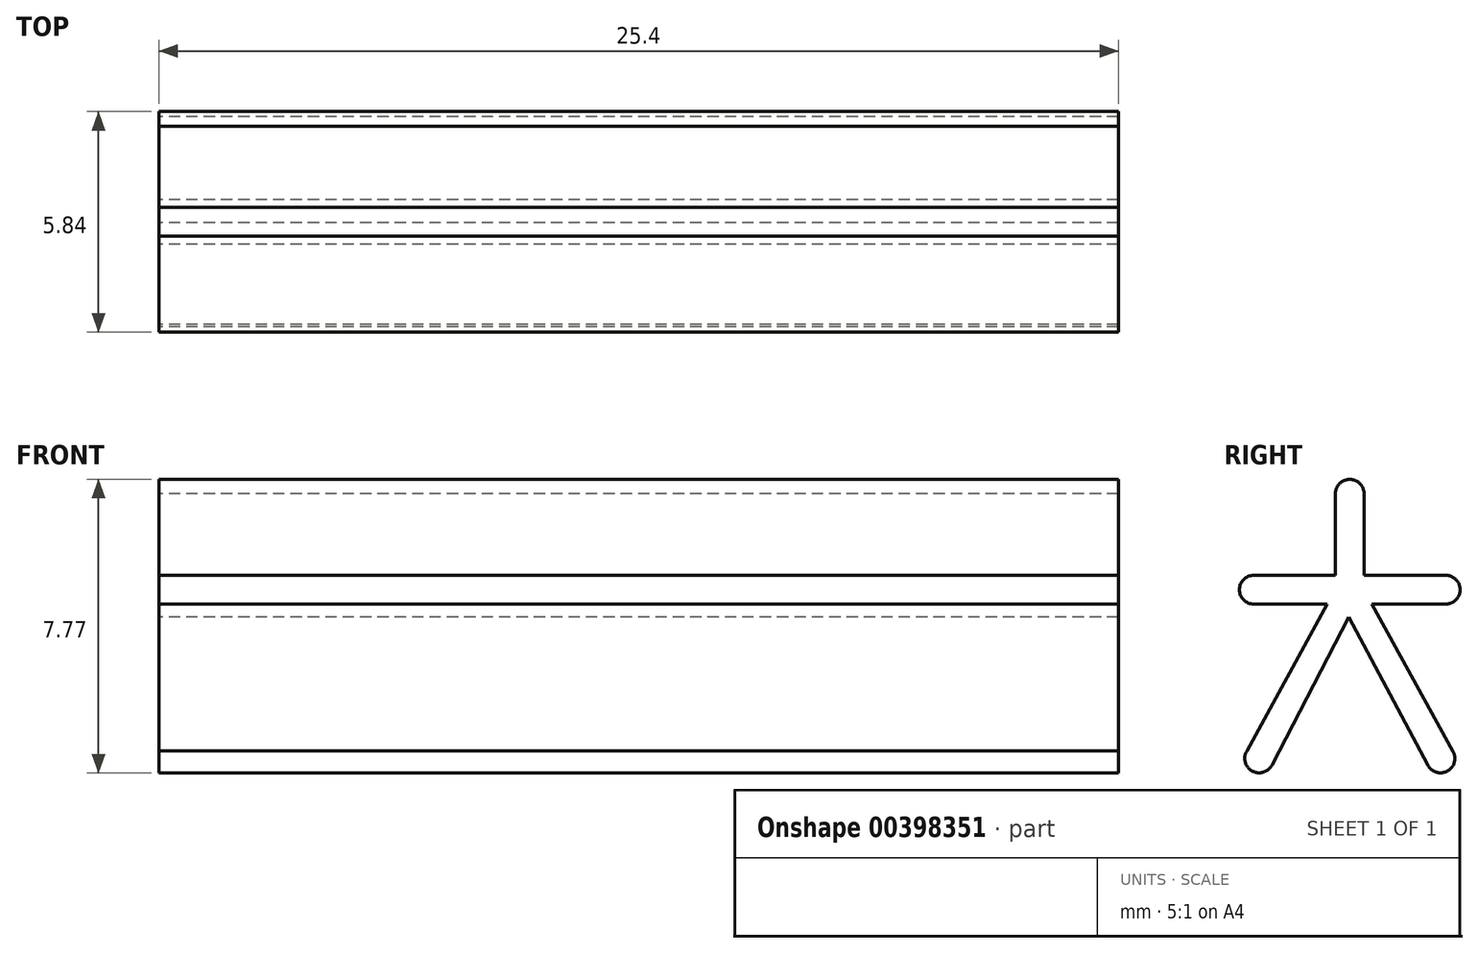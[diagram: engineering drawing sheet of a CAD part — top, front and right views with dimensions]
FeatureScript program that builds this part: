
annotation { "Feature Type Name" : "Feature", "Feature Type Description" : "" }
export const myFeature = defineFeature(function(context is Context, id is Id, definition is map)
    precondition{}
    {
        {
            var Q0;
            Q0=qCreatedBy(makeId("Right.planeOp"),FACE);
            var sketch = newSketch(context, id + "F0", { "sketchPlane" : qUnion([Q0])});
            skLineSegment(sketch, "E0", {"start": v(0, 0) * mm, "end": v(0, 2.54) * mm});
            skLineSegment(sketch, "E1", {"start": v(0, 0) * mm, "end": v(2.54, 0) * mm});
            skLineSegment(sketch, "E2", {"start": v(0, 0) * mm, "end": v(-2.54, 0) * mm});
            skLineSegment(sketch, "E3", {"start": v(0, 0) * mm, "end": v(-2.4, -4.47) * mm});
            skLineSegment(sketch, "E4", {"start": v(0, 0) * mm, "end": v(2.4, -4.47) * mm});
            skCircle(sketch, "E5", {"center": v(0, 0) * mm, "radius": 0.38 * mm});
            skCircle(sketch, "E6", {"center": v(0, 2.54) * mm, "radius": 0.38 * mm});
            skCircle(sketch, "E7", {"center": v(2.54, 0) * mm, "radius": 0.38 * mm});
            skCircle(sketch, "E8", {"center": v(2.4, -4.47) * mm, "radius": 0.38 * mm});
            skCircle(sketch, "E9", {"center": v(-2.4, -4.47) * mm, "radius": 0.38 * mm});
            skCircle(sketch, "E10", {"center": v(-2.54, 0) * mm, "radius": 0.38 * mm});
            skLineSegment(sketch, "E11", {"start": v(0.38, 2.53) * mm, "end": v(0.38, 0) * mm});
            skLineSegment(sketch, "E12", {"start": v(-0.38, 2.54) * mm, "end": v(-0.38, 0) * mm});
            skLineSegment(sketch, "E13", {"start": v(2.53, 0.38) * mm, "end": v(0, 0.38) * mm});
            skLineSegment(sketch, "E14", {"start": v(0, -0.38) * mm, "end": v(2.54, -0.38) * mm});
            skLineSegment(sketch, "E15", {"start": v(0, -0.38) * mm, "end": v(-2.54, -0.38) * mm});
            skLineSegment(sketch, "E16", {"start": v(0, 0.38) * mm, "end": v(-2.54, 0.38) * mm});
            skLineSegment(sketch, "E17", {"start": v(-2.72, -4.26) * mm, "end": v(-0.38, 0) * mm});
            skLineSegment(sketch, "E18", {"start": v(0.38, 0) * mm, "end": v(2.74, -4.28) * mm});
            skLineSegment(sketch, "E19", {"start": v(-0.2, -0.38) * mm, "end": v(2.07, -4.65) * mm});
            skLineSegment(sketch, "E20", {"start": v(0.18, -0.34) * mm, "end": v(-2.06, -4.65) * mm});
            skSolve(sketch);
        }
        {
            var Q0;
            {var subQ3=sQuery(id+"F0.wireOp",EDGE,"E7");var subQ5=sQuery(id+"F0.wireOp",EDGE,"E14");var subQ6=makeQuery(id+"F0.imprint","INTERSECT",VERTEX,{"derivedFrom":[subQ3,subQ5]});Q0=makeQuery(id+"F0.imprint","IMPRINT",FACE,{"disambiguationData":[TD([[makeQuery(id+"F0.imprint","IMPRINT",EDGE,{"disambiguationData":[TD([[subQ6,1.0]])],"derivedFrom":subQ3}),-1.0]])]});}
            var Q1;
            {var subQ3=sQuery(id+"F0.wireOp",EDGE,"E10");var subQ5=sQuery(id+"F0.wireOp",EDGE,"E16");var subQ6=makeQuery(id+"F0.imprint","INTERSECT",VERTEX,{"derivedFrom":[subQ3,subQ5]});Q1=makeQuery(id+"F0.imprint","IMPRINT",FACE,{"disambiguationData":[TD([[makeQuery(id+"F0.imprint","IMPRINT",EDGE,{"disambiguationData":[TD([[subQ6,1.0]])],"derivedFrom":subQ3}),-1.0]])]});}
            var Q2;
            {var subQ3=sQuery(id+"F0.wireOp",EDGE,"E10");var subQ5=sQuery(id+"F0.wireOp",EDGE,"E15");var subQ6=makeQuery(id+"F0.imprint","INTERSECT",VERTEX,{"derivedFrom":[subQ3,subQ5]});Q2=makeQuery(id+"F0.imprint","IMPRINT",FACE,{"disambiguationData":[TD([[makeQuery(id+"F0.imprint","IMPRINT",EDGE,{"disambiguationData":[TD([[subQ6,-1.0]])],"derivedFrom":subQ3}),-1.0]])]});}
            var Q3;
            {var subQ3=sQuery(id+"F0.wireOp",EDGE,"E7");var subQ5=sQuery(id+"F0.wireOp",EDGE,"E13");var subQ6=makeQuery(id+"F0.imprint","INTERSECT",VERTEX,{"derivedFrom":[subQ3,subQ5]});Q3=makeQuery(id+"F0.imprint","IMPRINT",FACE,{"disambiguationData":[TD([[makeQuery(id+"F0.imprint","IMPRINT",EDGE,{"disambiguationData":[TD([[subQ6,-1.0]])],"derivedFrom":subQ3}),-1.0]])]});}
            var Q4;
            {var subQ0=sQuery(id+"F0.wireOp",EDGE,"E8");var subQ1=sQuery(id+"F0.wireOp",EDGE,"E4");var subQ2=makeQuery(id+"F0.imprint","INTERSECT",VERTEX,{"derivedFrom":[subQ1,subQ0]});Q4=makeQuery(id+"F0.imprint","IMPRINT",FACE,{"disambiguationData":[TD([[makeQuery(id+"F0.imprint","IMPRINT",EDGE,{"disambiguationData":[TD([[subQ2,1.0]])],"derivedFrom":subQ1}),1.0]])]});}
            var Q5;
            {var subQ3=sQuery(id+"F0.wireOp",EDGE,"E14");var subQ5=sQuery(id+"F0.wireOp",EDGE,"E18");var subQ7=makeQuery(id+"F0.imprint","INTERSECT",VERTEX,{"derivedFrom":[subQ3,subQ5]});Q5=makeQuery(id+"F0.imprint","IMPRINT",FACE,{"disambiguationData":[TD([[makeQuery(id+"F0.imprint","IMPRINT",EDGE,{"disambiguationData":[TD([[subQ7,1.0]])],"derivedFrom":subQ3}),1.0]])]});}
            var Q6;
            {var subQ3=sQuery(id+"F0.wireOp",EDGE,"E9");var subQ5=sQuery(id+"F0.wireOp",EDGE,"E17");var subQ6=makeQuery(id+"F0.imprint","INTERSECT",VERTEX,{"derivedFrom":[subQ3,subQ5]});Q6=makeQuery(id+"F0.imprint","IMPRINT",FACE,{"disambiguationData":[TD([[makeQuery(id+"F0.imprint","IMPRINT",EDGE,{"disambiguationData":[TD([[subQ6,1.0]])],"derivedFrom":subQ3}),-1.0]])]});}
            var Q7;
            {var subQ0=sQuery(id+"F0.wireOp",EDGE,"E6");var subQ1=makeQuery(id+"F0.imprint","INTERSECT",VERTEX,{"derivedFrom":[subQ0,sQuery(id+"F0.wireOp",EDGE,"E12")]});Q7=makeQuery(id+"F0.imprint","IMPRINT",FACE,{"disambiguationData":[TD([[makeQuery(id+"F0.imprint","IMPRINT",EDGE,{"disambiguationData":[TD([[subQ1,-1.0]])],"derivedFrom":subQ0}),1.0]])]});}
            var Q8;
            {var subQ0=sQuery(id+"F0.wireOp",EDGE,"E9");var subQ1=makeQuery(id+"F0.imprint","INTERSECT",VERTEX,{"derivedFrom":[subQ0,sQuery(id+"F0.wireOp",EDGE,"E17")]});Q8=makeQuery(id+"F0.imprint","IMPRINT",FACE,{"disambiguationData":[TD([[makeQuery(id+"F0.imprint","IMPRINT",EDGE,{"disambiguationData":[TD([[subQ1,1.0]])],"derivedFrom":subQ0}),1.0]])]});}
            var Q9;
            {var subQ1=sQuery(id+"F0.wireOp",EDGE,"E8");var subQ6=sQuery(id+"F0.wireOp",EDGE,"E4");var subQ9=makeQuery(id+"F0.imprint","INTERSECT",VERTEX,{"derivedFrom":[subQ6,subQ1]});Q9=makeQuery(id+"F0.imprint","IMPRINT",FACE,{"disambiguationData":[TD([[makeQuery(id+"F0.imprint","IMPRINT",EDGE,{"disambiguationData":[TD([[subQ9,1.0]])],"derivedFrom":subQ6}),-1.0]])]});}
            var Q10;
            {var subQ0=sQuery(id+"F0.wireOp",EDGE,"E8");var subQ1=makeQuery(id+"F0.imprint","INTERSECT",VERTEX,{"derivedFrom":[subQ0,sQuery(id+"F0.wireOp",EDGE,"E18")]});Q10=makeQuery(id+"F0.imprint","IMPRINT",FACE,{"disambiguationData":[TD([[makeQuery(id+"F0.imprint","IMPRINT",EDGE,{"disambiguationData":[TD([[subQ1,-1.0]])],"derivedFrom":subQ0}),1.0]])]});}
            var Q11;
            {var subQ0=sQuery(id+"F0.wireOp",EDGE,"E10");var subQ1=makeQuery(id+"F0.imprint","INTERSECT",VERTEX,{"derivedFrom":[subQ0,sQuery(id+"F0.wireOp",EDGE,"E16")]});Q11=makeQuery(id+"F0.imprint","IMPRINT",FACE,{"disambiguationData":[TD([[makeQuery(id+"F0.imprint","IMPRINT",EDGE,{"disambiguationData":[TD([[subQ1,1.0]])],"derivedFrom":subQ0}),1.0]])]});}
            var Q12;
            {var subQ3=sQuery(id+"F0.wireOp",EDGE,"E6");var subQ5=sQuery(id+"F0.wireOp",EDGE,"E12");var subQ7=makeQuery(id+"F0.imprint","INTERSECT",VERTEX,{"derivedFrom":[subQ3,subQ5]});Q12=makeQuery(id+"F0.imprint","IMPRINT",FACE,{"disambiguationData":[TD([[makeQuery(id+"F0.imprint","IMPRINT",EDGE,{"disambiguationData":[TD([[subQ7,-1.0]])],"derivedFrom":subQ3}),-1.0]])]});}
            var Q13;
            {var subQ3=sQuery(id+"F0.wireOp",EDGE,"E9");var subQ5=sQuery(id+"F0.wireOp",EDGE,"E20");var subQ6=makeQuery(id+"F0.imprint","INTERSECT",VERTEX,{"derivedFrom":[subQ3,subQ5]});Q13=makeQuery(id+"F0.imprint","IMPRINT",FACE,{"disambiguationData":[TD([[makeQuery(id+"F0.imprint","IMPRINT",EDGE,{"disambiguationData":[TD([[subQ6,-1.0]])],"derivedFrom":subQ3}),-1.0]])]});}
            var Q14;
            {var subQ0=sQuery(id+"F0.wireOp",EDGE,"E7");var subQ1=makeQuery(id+"F0.imprint","INTERSECT",VERTEX,{"derivedFrom":[subQ0,sQuery(id+"F0.wireOp",EDGE,"E13")]});Q14=makeQuery(id+"F0.imprint","IMPRINT",FACE,{"disambiguationData":[TD([[makeQuery(id+"F0.imprint","IMPRINT",EDGE,{"disambiguationData":[TD([[subQ1,-1.0]])],"derivedFrom":subQ0}),1.0]])]});}
            var Q15;
            {var subQ1=sQuery(id+"F0.wireOp",EDGE,"E3");var subQ3=sQuery(id+"F0.wireOp",EDGE,"E5");var subQ4=makeQuery(id+"F0.imprint","INTERSECT",VERTEX,{"derivedFrom":[subQ1,subQ3]});Q15=makeQuery(id+"F0.imprint","IMPRINT",FACE,{"disambiguationData":[TD([[makeQuery(id+"F0.imprint","IMPRINT",EDGE,{"disambiguationData":[TD([[subQ4,-1.0]])],"derivedFrom":subQ1}),-1.0]])]});}
            var Q16;
            {var subQ3=sQuery(id+"F0.wireOp",EDGE,"E6");var subQ5=sQuery(id+"F0.wireOp",EDGE,"E11");var subQ6=makeQuery(id+"F0.imprint","INTERSECT",VERTEX,{"derivedFrom":[subQ3,subQ5]});Q16=makeQuery(id+"F0.imprint","IMPRINT",FACE,{"disambiguationData":[TD([[makeQuery(id+"F0.imprint","IMPRINT",EDGE,{"disambiguationData":[TD([[subQ6,1.0]])],"derivedFrom":subQ3}),-1.0]])]});}
            var Q17;
            {var subQ3=sQuery(id+"F0.wireOp",EDGE,"E20");var subQ5=sQuery(id+"F0.wireOp",EDGE,"E19");var subQ7=makeQuery(id+"F0.imprint","INTERSECT",VERTEX,{"derivedFrom":[subQ5,subQ3]});Q17=makeQuery(id+"F0.imprint","IMPRINT",FACE,{"disambiguationData":[TD([[makeQuery(id+"F0.imprint","IMPRINT",EDGE,{"disambiguationData":[TD([[subQ7,1.0]])],"derivedFrom":subQ3}),-1.0]])]});}
            var Q18;
            {var subQ1=sQuery(id+"F0.wireOp",EDGE,"E3");var subQ3=sQuery(id+"F0.wireOp",EDGE,"E5");var subQ4=makeQuery(id+"F0.imprint","INTERSECT",VERTEX,{"derivedFrom":[subQ1,subQ3]});Q18=makeQuery(id+"F0.imprint","IMPRINT",FACE,{"disambiguationData":[TD([[makeQuery(id+"F0.imprint","IMPRINT",EDGE,{"disambiguationData":[TD([[subQ4,-1.0]])],"derivedFrom":subQ1}),1.0]])]});}
            var Q19;
            {var subQ0=sQuery(id+"F0.wireOp",EDGE,"E3");var subQ3=sQuery(id+"F0.wireOp",EDGE,"E5");var subQ5=makeQuery(id+"F0.imprint","INTERSECT",VERTEX,{"derivedFrom":[subQ0,subQ3]});Q19=makeQuery(id+"F0.imprint","IMPRINT",FACE,{"disambiguationData":[TD([[makeQuery(id+"F0.imprint","IMPRINT",EDGE,{"disambiguationData":[TD([[subQ5,1.0]])],"derivedFrom":subQ3}),1.0]])]});}
            var Q20;
            {var subQ1=sQuery(id+"F0.wireOp",EDGE,"E4");var subQ3=sQuery(id+"F0.wireOp",EDGE,"E14");var subQ4=makeQuery(id+"F0.imprint","INTERSECT",VERTEX,{"derivedFrom":[subQ1,subQ3]});Q20=makeQuery(id+"F0.imprint","IMPRINT",FACE,{"disambiguationData":[TD([[makeQuery(id+"F0.imprint","IMPRINT",EDGE,{"disambiguationData":[TD([[subQ4,1.0]])],"derivedFrom":subQ3}),1.0]])]});}
            var Q21;
            {var subQ0=sQuery(id+"F0.wireOp",EDGE,"E2");var subQ3=sQuery(id+"F0.wireOp",EDGE,"E5");var subQ5=makeQuery(id+"F0.imprint","INTERSECT",VERTEX,{"derivedFrom":[subQ0,subQ3,sQuery(id+"F0.wireOp",EDGE,"E12"),sQuery(id+"F0.wireOp",EDGE,"E17")]});Q21=makeQuery(id+"F0.imprint","IMPRINT",FACE,{"disambiguationData":[TD([[makeQuery(id+"F0.imprint","IMPRINT",EDGE,{"disambiguationData":[TD([[subQ5,1.0]])],"derivedFrom":subQ3}),1.0]])]});}
            var Q22;
            {var subQ0=sQuery(id+"F0.wireOp",EDGE,"E1");var subQ3=sQuery(id+"F0.wireOp",EDGE,"E5");var subQ5=makeQuery(id+"F0.imprint","INTERSECT",VERTEX,{"derivedFrom":[subQ0,subQ3,sQuery(id+"F0.wireOp",EDGE,"E11"),sQuery(id+"F0.wireOp",EDGE,"E18")]});Q22=makeQuery(id+"F0.imprint","IMPRINT",FACE,{"disambiguationData":[TD([[makeQuery(id+"F0.imprint","IMPRINT",EDGE,{"disambiguationData":[TD([[subQ5,-1.0]])],"derivedFrom":subQ3}),1.0]])]});}
            var Q23;
            {var subQ0=sQuery(id+"F0.wireOp",EDGE,"E11");var subQ3=sQuery(id+"F0.wireOp",EDGE,"E13");var subQ5=makeQuery(id+"F0.imprint","INTERSECT",VERTEX,{"derivedFrom":[subQ0,subQ3]});Q23=makeQuery(id+"F0.imprint","IMPRINT",FACE,{"disambiguationData":[TD([[makeQuery(id+"F0.imprint","IMPRINT",EDGE,{"disambiguationData":[TD([[subQ5,-1.0]])],"derivedFrom":subQ0}),-1.0]])]});}
            var Q24;
            {var subQ0=sQuery(id+"F0.wireOp",EDGE,"E4");var subQ3=sQuery(id+"F0.wireOp",EDGE,"E5");var subQ5=makeQuery(id+"F0.imprint","INTERSECT",VERTEX,{"derivedFrom":[subQ0,subQ3,sQuery(id+"F0.wireOp",EDGE,"E20")]});Q24=makeQuery(id+"F0.imprint","IMPRINT",FACE,{"disambiguationData":[TD([[makeQuery(id+"F0.imprint","IMPRINT",EDGE,{"disambiguationData":[TD([[subQ5,-1.0]])],"derivedFrom":subQ3}),1.0]])]});}
            var Q25;
            {var subQ1=sQuery(id+"F0.wireOp",EDGE,"E3");var subQ3=sQuery(id+"F0.wireOp",EDGE,"E5");var subQ4=makeQuery(id+"F0.imprint","INTERSECT",VERTEX,{"derivedFrom":[subQ1,subQ3]});Q25=makeQuery(id+"F0.imprint","IMPRINT",FACE,{"disambiguationData":[TD([[makeQuery(id+"F0.imprint","IMPRINT",EDGE,{"disambiguationData":[TD([[subQ4,-1.0]])],"derivedFrom":subQ3}),1.0]])]});}
            var Q26;
            {var subQ0=sQuery(id+"F0.wireOp",EDGE,"E12");var subQ3=sQuery(id+"F0.wireOp",EDGE,"E16");var subQ5=makeQuery(id+"F0.imprint","INTERSECT",VERTEX,{"derivedFrom":[subQ0,subQ3]});Q26=makeQuery(id+"F0.imprint","IMPRINT",FACE,{"disambiguationData":[TD([[makeQuery(id+"F0.imprint","IMPRINT",EDGE,{"disambiguationData":[TD([[subQ5,-1.0]])],"derivedFrom":subQ0}),1.0]])]});}
            var Q27;
            {var subQ0=sQuery(id+"F0.wireOp",EDGE,"E14");var subQ3=sQuery(id+"F0.wireOp",EDGE,"E20");var subQ5=makeQuery(id+"F0.imprint","INTERSECT",VERTEX,{"derivedFrom":[subQ0,subQ3]});Q27=makeQuery(id+"F0.imprint","IMPRINT",FACE,{"disambiguationData":[TD([[makeQuery(id+"F0.imprint","IMPRINT",EDGE,{"disambiguationData":[TD([[subQ5,1.0]])],"derivedFrom":subQ0}),1.0]])]});}
            extrude(context, id + "F1", {"entities" : qUnion([Q0, Q1, Q2, Q3, Q4, Q5, Q6, Q7, Q8, Q9, Q10, Q11, Q12, Q13, Q14, Q15, Q16, Q17, Q18, Q19, Q20, Q21, Q22, Q23, Q24, Q25, Q26, Q27]), "depth" : 25.4 * mm});
        }
    });
